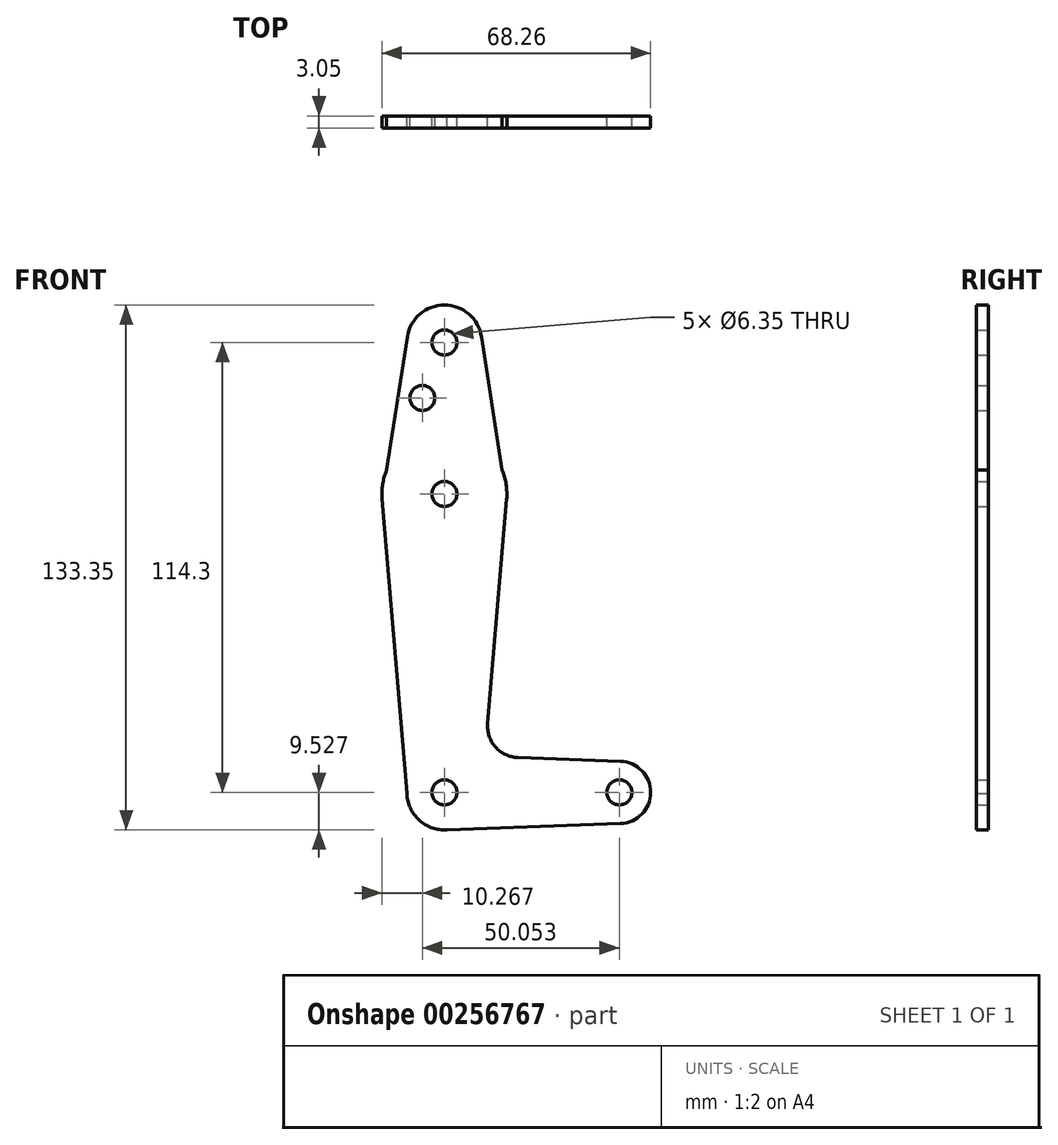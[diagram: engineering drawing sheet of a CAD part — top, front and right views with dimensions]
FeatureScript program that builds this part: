
annotation { "Feature Type Name" : "Feature", "Feature Type Description" : "" }
export const myFeature = defineFeature(function(context is Context, id is Id, definition is map)
    precondition{}
    {
        {
            var Q0;
            Q0=qCreatedBy(makeId("Front.planeOp"),FACE);
            var sketch = newSketch(context, id + "F0", { "sketchPlane" : qUnion([Q0])});
            skLineSegment(sketch, "E0", {"start": v(0, 79.24) * mm, "end": v(0, -35.06) * mm});
            skLineSegment(sketch, "E1", {"start": v(0, -35.06) * mm, "end": v(44.45, -35.06) * mm});
            skCircle(sketch, "E2", {"center": v(0, 79.24) * mm, "radius": 9.53 * mm});
            skCircle(sketch, "E3", {"center": v(0, -35.06) * mm, "radius": 9.53 * mm});
            skCircle(sketch, "E4", {"center": v(44.45, -35.06) * mm, "radius": 0.8 * mm});
            skCircle(sketch, "E5", {"center": v(44.45, -35.06) * mm, "radius": 7.94 * mm});
            skCircle(sketch, "E6", {"center": v(0, 40.76) * mm, "radius": 15.88 * mm});
            skLineSegment(sketch, "E7", {"start": v(-9.52, -35.37) * mm, "end": v(-15.82, 39.43) * mm});
            skLineSegment(sketch, "E8", {"start": v(11, -17.59) * mm, "end": v(15.82, 39.42) * mm});
            skLineSegment(sketch, "E9", {"start": v(-9.41, 80.7) * mm, "end": v(-15.82, 39.43) * mm});
            skLineSegment(sketch, "E10", {"start": v(9.41, 80.7) * mm, "end": v(15.82, 39.42) * mm});
            skLineSegment(sketch, "E11", {"start": v(18.64, -26.2) * mm, "end": v(44.73, -27.13) * mm});
            skLineSegment(sketch, "E12", {"start": v(0, -44.59) * mm, "end": v(44.73, -43) * mm});
            skCircle(sketch, "E13", {"center": v(0, 79.24) * mm, "radius": 3.18 * mm});
            skCircle(sketch, "E14", {"center": v(0, 40.76) * mm, "radius": 3.18 * mm});
            skCircle(sketch, "E15", {"center": v(0, -35.06) * mm, "radius": 3.18 * mm});
            skCircle(sketch, "E16", {"center": v(44.45, -35.06) * mm, "radius": 3.18 * mm});
            skArc(sketch, "E17.filletArc", {"start": v(11, -17.59) * mm, "mid": v(12.98, -23.53) * mm, "end": v(18.64, -26.2) * mm});
            skCircle(sketch, "E18", {"center": v(-5.6, 65.17) * mm, "radius": 3.18 * mm});
            skSolve(sketch);
        }
        {
            var Q0;
            Q0 = qSketchRegion(id + "F0", true);
            extrude(context, id + "F1", {"entities" : qUnion([Q0]), "depth" : 3.05 * mm});
        }
        {
            var Q0;
            {var subQ0=sQuery(id+"F0.wireOp",EDGE,"E3");var subQ1=sQuery(id+"F0.wireOp",EDGE,"E0");var subQ2=makeQuery(id+"F0.imprint","INTERSECT",VERTEX,{"derivedFrom":[subQ1,subQ0]});Q0=makeQuery(id+"F0.imprint","IMPRINT",FACE,{"disambiguationData":[TD([[makeQuery(id+"F0.imprint","IMPRINT",EDGE,{"disambiguationData":[TD([[subQ2,-1.0]])],"derivedFrom":subQ1}),1.0]])]});}
            extrude(context, id + "F2", {"entities" : qUnion([Q0]), "operationType" : NewBodyOperationType.ADD, "depth" : 3.05 * mm});
        }
    });
